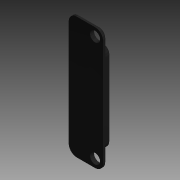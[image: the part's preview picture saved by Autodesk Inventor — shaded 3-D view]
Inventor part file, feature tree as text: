
AUTODESK INVENTOR PART (.ipt)
format: ipt  version: 2013 (Build 170138000, 138)  size: 152,576 bytes
history: native  units: in
note: dims shown in document units (in); Inventor stores cm internally (conversion verified against a paired STEP export)
features: extrude x2, sketch x2, reference x2, chamfer x1
ambient origin geometry x8: Origin, YZ Plane, XZ Plane, XY Plane, X Axis, Y Axis, Z Axis, Center Point
bodies: Solid1 (feature_tree)
feature tree (7):
  extrude  "Extrusion1"  Depth=0.0394in TaperAngle=0.0deg
  extrude  "Extrusion2"  Depth=0.1575in
  chamfer  "Chamfer1"  Distance=0.1575in
  sketch  "Sketch1"  dims[d0=0.0787in d1=0.0394in d2=0.0in]
  reference  "Reference1"
  reference  "Reference2"
  sketch  "Sketch2"  dims[d3=0.0787in d4=0.1575in d5=0.1575in d6=0.0394in d7=0.0in d8=0.0197in d9=0.0787in d10=45.0deg]
